# Revit family: SPF170L
name_source: partatom
category: Detail Items
revit_build: Autodesk Revit 2016 (Build: 20150220_1215(x64)
units: mm (PartAtom-declared; Revit-internal decimal feet)

## family parameters
OmniClass Number = 23.20.40.11.24.14
OmniClass Title = Wood Connectors
Rotate with component = No
Shared = No

## types (1)
- SST_XXX_Template
    Density = 0.00 kg
    Description = Screws
    EPD = https://www.strongtie.eu
    ETA / DoP = https://www.strongtie.eu
    Manufacturer = Simpson Strong-Tie
    Model = AB90
    Model Disclaimer = Contact Simpson Strong-Tie Company  for more information
    Name = AB90
    ObjectType = AB90
    Product Material = Galvanised
    Product Type = Screws
    Reference = --
    Technical datasheet = https://www.strongtie.eu
    URL = www.strongtie.eu
    UniClass Number = Pr_20_29_76_98
    UniClass Title = Wood screws
    _visiblefront = No
    _visibleleft = No
    _visibleright = No
    _visibletop = No

## geometry (parser evidence)
native form markers: Sweep x2
no freeform markers — native parametric forms only
